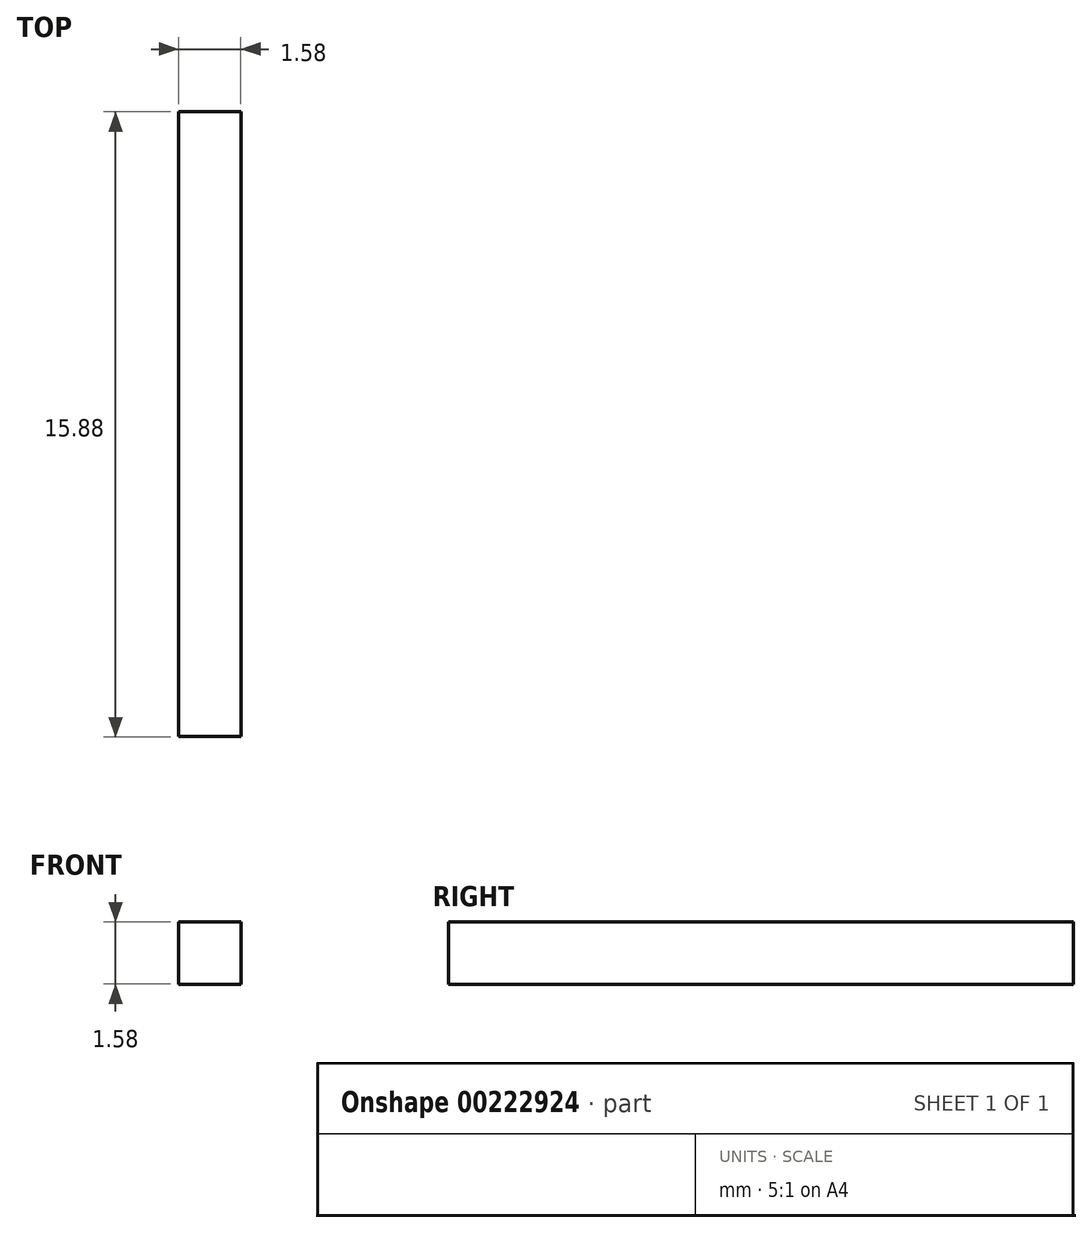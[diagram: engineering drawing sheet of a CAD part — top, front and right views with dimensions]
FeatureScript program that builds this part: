
annotation { "Feature Type Name" : "Feature", "Feature Type Description" : "" }
export const myFeature = defineFeature(function(context is Context, id is Id, definition is map)
    precondition{}
    {
        {
            var Q0;
            Q0=qCreatedBy(makeId("Front.planeOp"),FACE);
            var sketch = newSketch(context, id + "F0", { "sketchPlane" : qUnion([Q0])});
            skLineSegment(sketch, "E0.bottom", {"start": v(-2.38, 2.38) * mm, "end": v(2.38, 2.38) * mm});
            skLineSegment(sketch, "E0.top", {"start": v(-2.38, -2.38) * mm, "end": v(2.38, -2.38) * mm});
            skLineSegment(sketch, "E0.left", {"start": v(-2.38, 2.38) * mm, "end": v(-2.38, -2.38) * mm});
            skLineSegment(sketch, "E0.right", {"start": v(2.38, 2.38) * mm, "end": v(2.38, -2.38) * mm});
            skPoint(sketch, "E0.middle", {"position": v(0, 0) * mm});
            skLineSegment(sketch, "E1.bottom", {"start": v(-0.8, 2.38) * mm, "end": v(0.8, 2.38) * mm});
            skLineSegment(sketch, "E1.top", {"start": v(-0.8, -2.38) * mm, "end": v(0.8, -2.38) * mm});
            skLineSegment(sketch, "E1.left", {"start": v(-0.8, 2.38) * mm, "end": v(-0.8, -2.38) * mm});
            skLineSegment(sketch, "E1.right", {"start": v(0.8, 2.38) * mm, "end": v(0.8, -2.38) * mm});
            skLineSegment(sketch, "E2.bottom", {"start": v(-2.38, 0.8) * mm, "end": v(2.38, 0.8) * mm});
            skLineSegment(sketch, "E2.top", {"start": v(-2.38, -0.8) * mm, "end": v(2.38, -0.8) * mm});
            skLineSegment(sketch, "E2.left", {"start": v(-2.38, 0.8) * mm, "end": v(-2.38, -0.8) * mm});
            skLineSegment(sketch, "E2.right", {"start": v(2.38, 0.8) * mm, "end": v(2.38, -0.8) * mm});
            skSolve(sketch);
        }
        {
            var Q0;
            {var subQ5=sQuery(id+"F0.wireOp",EDGE,"E2.left");Q0=makeQuery(id+"F0.imprint","IMPRINT",FACE,{"disambiguationData":[TD([[makeQuery(id+"F0.imprint","IMPRINT",EDGE,{"derivedFrom":subQ5}),1.0]])]});}
            var Q1;
            {var subQ0=sQuery(id+"F0.wireOp",EDGE,"E1.bottom");Q1=makeQuery(id+"F0.imprint","IMPRINT",FACE,{"disambiguationData":[TD([[makeQuery(id+"F0.imprint","IMPRINT",EDGE,{"derivedFrom":subQ0}),-1.0]])]});}
            var Q2;
            {var subQ0=sQuery(id+"F0.wireOp",EDGE,"E2.bottom");var subQ1=sQuery(id+"F0.wireOp",EDGE,"E1.left");var subQ2=makeQuery(id+"F0.imprint","INTERSECT",VERTEX,{"derivedFrom":[subQ1,subQ0]});Q2=makeQuery(id+"F0.imprint","IMPRINT",FACE,{"disambiguationData":[TD([[makeQuery(id+"F0.imprint","IMPRINT",EDGE,{"disambiguationData":[TD([[subQ2,-1.0]])],"derivedFrom":subQ1}),1.0]])]});}
            var Q3;
            {var subQ5=sQuery(id+"F0.wireOp",EDGE,"E2.right");Q3=makeQuery(id+"F0.imprint","IMPRINT",FACE,{"disambiguationData":[TD([[makeQuery(id+"F0.imprint","IMPRINT",EDGE,{"derivedFrom":subQ5}),-1.0]])]});}
            var Q4;
            {var subQ0=sQuery(id+"F0.wireOp",EDGE,"E1.top");Q4=makeQuery(id+"F0.imprint","IMPRINT",FACE,{"disambiguationData":[TD([[makeQuery(id+"F0.imprint","IMPRINT",EDGE,{"derivedFrom":subQ0}),1.0]])]});}
            extrude(context, id + "F1", {"entities" : qUnion([Q0, Q1, Q2, Q3, Q4]), "depth" : 15.88 * mm});
        }
    });
